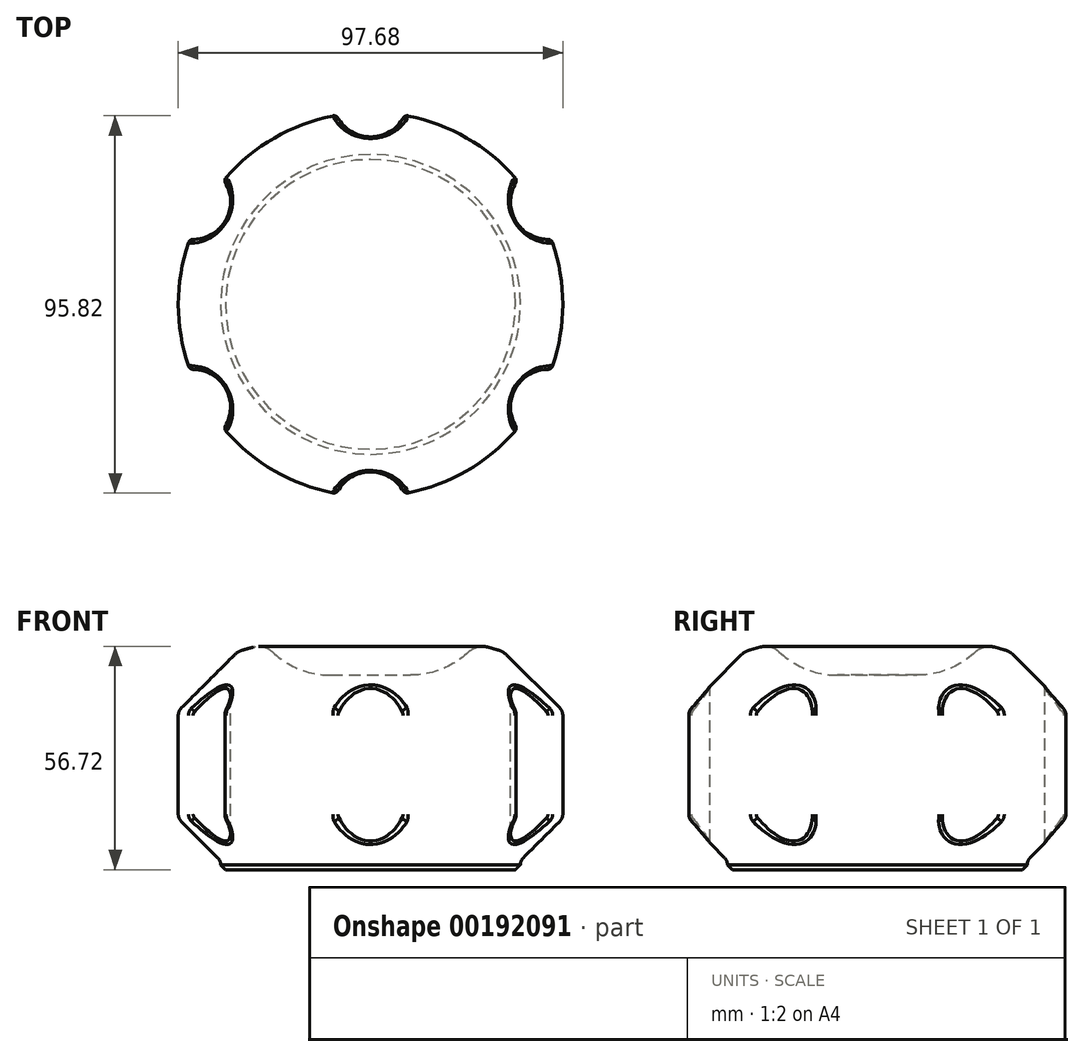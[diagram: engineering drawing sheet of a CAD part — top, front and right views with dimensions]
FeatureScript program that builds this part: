
annotation { "Feature Type Name" : "Feature", "Feature Type Description" : "" }
export const myFeature = defineFeature(function(context is Context, id is Id, definition is map)
    precondition{}
    {
        {
            var Q0;
            Q0=qCreatedBy(makeId("Front.planeOp"),FACE);
            var sketch = newSketch(context, id + "F0", { "sketchPlane" : qUnion([Q0])});
            skLineSegment(sketch, "E0", {"start": v(0, 0) * mm, "end": v(0, 57.3) * mm});
            skLineSegment(sketch, "E1", {"start": v(0, 57.3) * mm, "end": v(31.83, 57.3) * mm});
            skLineSegment(sketch, "E2", {"start": v(31.83, 57.3) * mm, "end": v(48.84, 40.3) * mm});
            skLineSegment(sketch, "E3", {"start": v(48.84, 40.3) * mm, "end": v(48.84, 13.06) * mm});
            skLineSegment(sketch, "E4", {"start": v(48.84, 13.06) * mm, "end": v(38.08, 2.3) * mm});
            skLineSegment(sketch, "E5", {"start": v(38.08, 2.3) * mm, "end": v(38.08, 0) * mm});
            skLineSegment(sketch, "E6", {"start": v(38.08, 0) * mm, "end": v(0, 0) * mm});
            skSolve(sketch);
        }
        {
            var Q0;
            Q0=makeQuery(id+"F0.imprint","IMPRINT",FACE,{"disambiguationData":[TD([[makeQuery(id+"F0.imprint","IMPRINT",EDGE,{"derivedFrom":sQuery(id+"F0.wireOp",EDGE,"E0")}),-1.0]])]});
            var Q1;
            Q1=sQuery(id+"F0.wireOp",EDGE,"E0");
            revolve(context, id + "F1", {"entities" : qUnion([Q0]), "axis" : qUnion([Q1]), "revolveType" : RevolveType.FULL});
        }
        {
            var Q0;
            Q0=makeQuery(id+"F1.opRevolve","SWEPT_EDGE",EDGE,{"disambiguationData":[OSD([sQuery(id+"F0.wireOp",EDGE,"E1"),sQuery(id+"F0.wireOp",EDGE,"E2")])]});
            chamfer(context, id + "F2", {"entities" : qUnion([Q0]), "chamferType" : ChamferType.OFFSET_ANGLE, "width" : 2.54 * mm, "oppositeDirection" : false, "angle" : 30 * degree, "tangentPropagation" : true});
        }
        {
            var Q0;
            Q0=makeQuery(id+"F1.opRevolve","SWEPT_EDGE",EDGE,{"disambiguationData":[OSD([sQuery(id+"F0.wireOp",EDGE,"E2"),sQuery(id+"F0.wireOp",EDGE,"E3")])]});
            var Q1;
            Q1=makeQuery(id+"F1.opRevolve","SWEPT_EDGE",EDGE,{"disambiguationData":[OSD([sQuery(id+"F0.wireOp",EDGE,"E3"),sQuery(id+"F0.wireOp",EDGE,"E4")])]});
            var Q2;
            Q2=makeQuery(id+"F1.opRevolve","SWEPT_EDGE",EDGE,{"disambiguationData":[OSD([sQuery(id+"F0.wireOp",EDGE,"E4"),sQuery(id+"F0.wireOp",EDGE,"E5")])]});
            fillet(context, id + "F3", {"entities" : qUnion([Q0, Q1, Q2]), "radius" : 2.54 * mm, "tangentPropagation" : true, "allowEdgeOverflow" : false});
        }
        {
            var Q0;
            Q0=makeQuery(id+"F1.opRevolve","SWEPT_FACE",FACE,{"disambiguationData":[OSD([sQuery(id+"F0.wireOp",EDGE,"E1")])]});
            extrude(context, id + "F4", {"entities" : qUnion([Q0]), "operationType" : NewBodyOperationType.REMOVE, "oppositeDirection" : true, "depth" : 7.87 * mm, "hasDraft" : true, "draftAngle" : 45 * degree, "draftPullDirection" : true});
        }
        {
            var Q0;
            Q0=makeQuery(id+"F4.boolean.opBoolean","COPY",EDGE,{"derivedFrom":makeQuery(id+"F4.opExtrude","CAP_EDGE",EDGE,{"disambiguationData":[OSD([sQuery(id+"F0.wireOp",EDGE,"E1"),sQuery(id+"F0.wireOp",EDGE,"E2")])],"isStart":false})});
            fillet(context, id + "F5", {"entities" : qUnion([Q0]), "radius" : 21.58 * mm, "tangentPropagation" : true, "allowEdgeOverflow" : false});
        }
        {
            var Q0;
            Q0=makeQuery(id+"F1.opRevolve","SWEPT_EDGE",EDGE,{"disambiguationData":[OSD([sQuery(id+"F0.wireOp",EDGE,"E5"),sQuery(id+"F0.wireOp",EDGE,"E6")])]});
            chamfer(context, id + "F6", {"entities" : qUnion([Q0]), "width" : 1.27 * mm, "tangentPropagation" : true});
        }
        {
            var Q0;
            {var subQ0=sQuery(id+"F0.wireOp",EDGE,"E2");Q0=makeQuery(id+"F2.opChamfer","BLEND_EDGE",EDGE,{"blendedFrom":[makeQuery(id+"F1.opRevolve","SWEPT_EDGE",EDGE,{"disambiguationData":[OSD([sQuery(id+"F0.wireOp",EDGE,"E1"),subQ0])]}),makeQuery(id+"F1.opRevolve","SWEPT_FACE",FACE,{"disambiguationData":[OSD([subQ0])]})],"blendedInto":[makeQuery(id+"F1.opRevolve","SWEPT_FACE",FACE,{"disambiguationData":[OSD([subQ0])]})]});}
            var Q1;
            {var subQ0=sQuery(id+"F0.wireOp",EDGE,"E2");var subQ1=sQuery(id+"F0.wireOp",EDGE,"E1");Q1=makeQuery(id+"F4.boolean.opBoolean","MERGE",EDGE,{"derivedFrom":[makeQuery(id+"F2.opChamfer","BLEND_EDGE",EDGE,{"blendedFrom":[makeQuery(id+"F1.opRevolve","SWEPT_EDGE",EDGE,{"disambiguationData":[OSD([subQ1,subQ0])]}),makeQuery(id+"F1.opRevolve","SWEPT_FACE",FACE,{"disambiguationData":[OSD([subQ1])]})],"blendedInto":[makeQuery(id+"F1.opRevolve","SWEPT_FACE",FACE,{"disambiguationData":[OSD([subQ1])]})]}),makeQuery(id+"F4.opExtrude","CAP_EDGE",EDGE,{"disambiguationData":[OSD([subQ1,subQ0])],"isStart":true})]});}
            fillet(context, id + "F7", {"entities" : qUnion([Q0, Q1]), "radius" : 5.08 * mm, "tangentPropagation" : true, "allowEdgeOverflow" : false});
        }
        {
            var Q0;
            Q0=qCreatedBy(makeId("Top.planeOp"),FACE);
            var sketch = newSketch(context, id + "F8", { "sketchPlane" : qUnion([Q0])});
            skLineSegment(sketch, "E7", {"start": v(0, 0) * mm, "end": v(0, 73.77) * mm});
            skCircle(sketch, "E8", {"center": v(0, 52.07) * mm, "radius": 9.53 * mm});
            skCircle(sketch, "E9.1.0", {"center": v(-45.1, 26.04) * mm, "radius": 9.53 * mm});
            skCircle(sketch, "E9.2.0", {"center": v(-45.1, -26.03) * mm, "radius": 9.53 * mm});
            skCircle(sketch, "E9.3.0", {"center": v(0, -52.07) * mm, "radius": 9.53 * mm});
            skCircle(sketch, "E9.4.0", {"center": v(45.1, -26.04) * mm, "radius": 9.53 * mm});
            skCircle(sketch, "E9.5.0", {"center": v(45.1, 26.04) * mm, "radius": 9.53 * mm});
            skPoint(sketch, "E9.center", {"position": v(0, 0) * mm});
            skSolve(sketch);
        }
        {
            var Q0;
            Q0 = qSketchRegion(id + "F8", true);
            extrude(context, id + "F9", {"entities" : qUnion([Q0]), "operationType" : NewBodyOperationType.REMOVE, "endBound" : BoundingType.THROUGH_ALL, "oppositeDirection" : true, "depth" : 25.4 * mm, "hasSecondDirection" : true, "secondDirectionBound" : SecondDirectionBoundingType.THROUGH_ALL, "secondDirectionOppositeDirection" : false, "secondDirectionDepth" : 25.4 * mm});
        }
        {
            var Q0;
            Q0=makeQuery(id+"F9.boolean.opBoolean","INTERSECT",EDGE,{"disambiguationData":[OD(0.0)],"derivedFrom":[makeQuery(id+"F1.opRevolve","SWEPT_FACE",FACE,{"disambiguationData":[OSD([sQuery(id+"F0.wireOp",EDGE,"E3")])]}),makeQuery(id+"F9.opExtrude","SWEPT_FACE",FACE,{"disambiguationData":[OSD([sQuery(id+"F8.wireOp",EDGE,"E9.2.0")])]})]});
            var Q1;
            Q1=makeQuery(id+"F9.boolean.opBoolean","COPY",FACE,{"derivedFrom":makeQuery(id+"F9.opExtrude","SWEPT_FACE",FACE,{"disambiguationData":[OSD([sQuery(id+"F8.wireOp",EDGE,"E9.3.0")])]})});
            var Q2;
            Q2=makeQuery(id+"F9.boolean.opBoolean","COPY",FACE,{"derivedFrom":makeQuery(id+"F9.opExtrude","SWEPT_FACE",FACE,{"disambiguationData":[OSD([sQuery(id+"F8.wireOp",EDGE,"E9.1.0")])]})});
            var Q3;
            Q3=makeQuery(id+"F9.boolean.opBoolean","COPY",FACE,{"derivedFrom":makeQuery(id+"F9.opExtrude","SWEPT_FACE",FACE,{"disambiguationData":[OSD([sQuery(id+"F8.wireOp",EDGE,"E8")])]})});
            var Q4;
            Q4=makeQuery(id+"F9.boolean.opBoolean","COPY",FACE,{"derivedFrom":makeQuery(id+"F9.opExtrude","SWEPT_FACE",FACE,{"disambiguationData":[OSD([sQuery(id+"F8.wireOp",EDGE,"E9.5.0")])]})});
            var Q5;
            Q5=makeQuery(id+"F9.boolean.opBoolean","COPY",FACE,{"derivedFrom":makeQuery(id+"F9.opExtrude","SWEPT_FACE",FACE,{"disambiguationData":[OSD([sQuery(id+"F8.wireOp",EDGE,"E9.4.0")])]})});
            fillet(context, id + "F10", {"entities" : qUnion([Q0, Q1, Q2, Q3, Q4, Q5]), "radius" : 1.27 * mm, "tangentPropagation" : true, "allowEdgeOverflow" : false});
        }
    });
